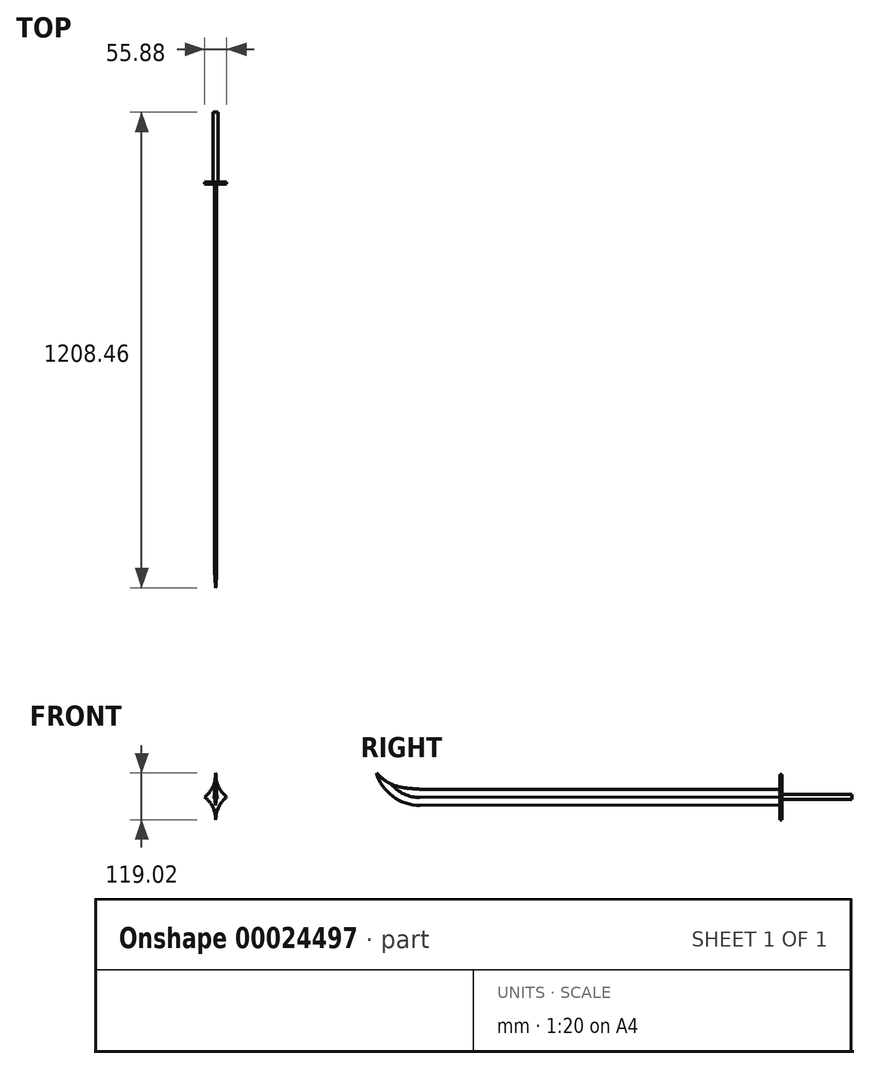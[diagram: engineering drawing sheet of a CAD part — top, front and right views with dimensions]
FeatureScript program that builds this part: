
annotation { "Feature Type Name" : "Feature", "Feature Type Description" : "" }
export const myFeature = defineFeature(function(context is Context, id is Id, definition is map)
    precondition{}
    {
        {
            var Q0;
            Q0=qCreatedBy(makeId("Right.planeOp"),FACE);
            var sketch = newSketch(context, id + "F0", { "sketchPlane" : qUnion([Q0])});
            skArc(sketch, "E0", {"start": v(0, 0) * mm, "mid": v(41.9, -59.69) * mm, "end": v(111.18, -82.52) * mm});
            skLineSegment(sketch, "E1", {"start": v(111.18, -82.52) * mm, "end": v(1025.58, -80.92) * mm});
            skLineSegment(sketch, "E2", {"start": v(111.18, -41.55) * mm, "end": v(1025.58, -41.55) * mm});
            skFitSpline(sketch, "E3", {"points": [v(0, 0) * mm, v(40.72, -30.05) * mm, v(111.18, -41.55) * mm], "startDerivative": vector(79.78, -75.94) * mm, "endDerivative": vector(140.83, -9.08) * mm});
            skLineSegment(sketch, "E4", {"start": v(1025.58, -41.55) * mm, "end": v(1025.58, -80.92) * mm});
            skSolve(sketch);
        }
        {
            var Q0;
            Q0 = qSketchRegion(id + "F0", true);
            extrude(context, id + "F1", {"entities" : qUnion([Q0]), "depth" : 5.08 * mm});
        }
        {
            var Q0;
            Q0=makeQuery(id+"F1.opExtrude","SWEPT_FACE",FACE,{"disambiguationData":[OSD([sQuery(id+"F0.wireOp",EDGE,"E4")])]});
            var sketch = newSketch(context, id + "F2", { "sketchPlane" : qUnion([Q0])});
            skLineSegment(sketch, "E5", {"start": v(-5.08, -61.2) * mm, "end": v(-2.54, -80.88) * mm});
            skLineSegment(sketch, "E6", {"start": v(0, -61.2) * mm, "end": v(-2.54, -80.88) * mm});
            skSolve(sketch);
        }
        {
            var Q0;
            {var subQ0=sQuery(id+"F2.wireOp",EDGE,"E5");Q0=makeQuery(id+"F2.imprint","IMPRINT",FACE,{"disambiguationData":[TD([[makeQuery(id+"F2.imprint","IMPRINT",EDGE,{"derivedFrom":subQ0}),-1.0]])]});}
            var Q1;
            {var subQ0=sQuery(id+"F2.wireOp",EDGE,"E6");Q1=makeQuery(id+"F2.imprint","IMPRINT",FACE,{"disambiguationData":[TD([[makeQuery(id+"F2.imprint","IMPRINT",EDGE,{"derivedFrom":subQ0}),1.0]])]});}
            var Q2;
            Q2=makeQuery(id+"F1.opExtrude","CAP_EDGE",EDGE,{"disambiguationData":[OSD([sQuery(id+"F0.wireOp",EDGE,"E1")])],"isStart":true});
            var Q3;
            Q3=makeQuery(id+"F1.opExtrude","CAP_EDGE",EDGE,{"disambiguationData":[OSD([sQuery(id+"F0.wireOp",EDGE,"E0")])],"isStart":true});
            sweep(context, id + "F3", {"operationType" : NewBodyOperationType.REMOVE, "profiles" : qUnion([Q0, Q1]), "path" : qUnion([Q2, Q3])});
        }
        {
            var Q0;
            Q0=makeQuery(id+"F1.opExtrude","SWEPT_FACE",FACE,{"disambiguationData":[OSD([sQuery(id+"F0.wireOp",EDGE,"E4")])]});
            var sketch = newSketch(context, id + "F4", { "sketchPlane" : qUnion([Q0])});
            skLineSegment(sketch, "E7", {"start": v(-2.54, -41.52) * mm, "end": v(-2.54, -3.42) * mm});
            skLineSegment(sketch, "E8", {"start": v(-2.54, -80.88) * mm, "end": v(-2.54, -118.98) * mm});
            skLineSegment(sketch, "E9", {"start": v(-5.08, -61.2) * mm, "end": v(-30.48, -61.2) * mm});
            skLineSegment(sketch, "E10", {"start": v(0, -61.2) * mm, "end": v(25.4, -61.2) * mm});
            skArc(sketch, "E11", {"start": v(-30.48, -61.2) * mm, "mid": v(-9.9, -35.5) * mm, "end": v(-2.54, -3.42) * mm});
            skArc(sketch, "E12", {"start": v(-2.54, -3.42) * mm, "mid": v(4.81, -35.5) * mm, "end": v(25.4, -61.2) * mm});
            skSolve(sketch);
        }
        {
            var Q0;
            Q0 = qSketchRegion(id + "F4", true);
            var Q1;
            {var subQ2=sQuery(id+"F4.wireOp",EDGE,"E7");Q1=makeQuery(id+"F4.imprint","IMPRINT",FACE,{"disambiguationData":[TD([[makeQuery(id+"F4.imprint","IMPRINT",EDGE,{"derivedFrom":subQ2}),1.0]])]});}
            var Q2;
            {var subQ2=sQuery(id+"F4.wireOp",EDGE,"E7");Q2=makeQuery(id+"F4.imprint","IMPRINT",FACE,{"disambiguationData":[TD([[makeQuery(id+"F4.imprint","IMPRINT",EDGE,{"derivedFrom":subQ2}),-1.0]])]});}
            var Q3;
            {var subQ0=sQuery(id+"F0.wireOp",EDGE,"E4");var subQ3=makeQuery(id+"F1.opExtrude","CAP_EDGE",EDGE,{"disambiguationData":[OSD([subQ0])],"isStart":true});Q3=makeQuery(id+"F4.imprint","IMPRINT",FACE,{"disambiguationData":[TD([[makeQuery(id+"F4.imprint","IMPRINT",EDGE,{"derivedFrom":subQ3}),-1.0]])]});}
            extrude(context, id + "F5", {"entities" : qUnion([Q0, Q1, Q2, Q3]), "depth" : 5.08 * mm});
        }
        {
            var Q0;
            Q0=makeQuery(id+"F5.opExtrude","SWEPT_BODY",BODY,{"disambiguationData":[OSD([sQuery(id+"F0.wireOp",EDGE,"E1"),sQuery(id+"F0.wireOp",EDGE,"E4"),sQuery(id+"F2.wireOp",EDGE,"E5"),sQuery(id+"F2.wireOp",EDGE,"E6"),sQuery(id+"F4.wireOp",EDGE,"E9"),sQuery(id+"F4.wireOp",EDGE,"E10"),sQuery(id+"F4.wireOp",EDGE,"E11"),sQuery(id+"F4.wireOp",EDGE,"E12")])]});
            var Q1;
            Q1=makeQuery(id+"F5.opExtrude","SWEPT_FACE",FACE,{"disambiguationData":[OSD([sQuery(id+"F4.wireOp",EDGE,"E9")])]});
            mirror(context, id + "F6", {"operationType" : NewBodyOperationType.ADD, "entities" : qUnion([Q0]), "mirrorPlane" : qUnion([Q1])});
        }
        {
            var Q0;
            {var subQ0=makeQuery(id+"F5.opExtrude","CAP_FACE",FACE,{"disambiguationData":[OSD([sQuery(id+"F0.wireOp",EDGE,"E1"),sQuery(id+"F0.wireOp",EDGE,"E4"),sQuery(id+"F2.wireOp",EDGE,"E5"),sQuery(id+"F2.wireOp",EDGE,"E6"),sQuery(id+"F4.wireOp",EDGE,"E9"),sQuery(id+"F4.wireOp",EDGE,"E10"),sQuery(id+"F4.wireOp",EDGE,"E11"),sQuery(id+"F4.wireOp",EDGE,"E12")])],"isStart":false});Q0=makeQuery(id+"F6.boolean.opBoolean","MERGE",FACE,{"derivedFrom":[subQ0,makeQuery(id+"F6.opPattern","COPY",FACE,{"derivedFrom":subQ0,"instanceName":"1"})]});}
            var sketch = newSketch(context, id + "F7", { "sketchPlane" : qUnion([Q0])});
            skLineSegment(sketch, "E13", {"start": v(-30.48, -61.2) * mm, "end": v(25.4, -61.2) * mm});
            skCircle(sketch, "E14", {"center": v(-2.54, -61.2) * mm, "radius": 6.35 * mm});
            skSolve(sketch);
        }
        {
            var Q0;
            Q0 = qSketchRegion(id + "F7", true);
            extrude(context, id + "F8", {"entities" : qUnion([Q0]), "operationType" : NewBodyOperationType.ADD, "depth" : 177.8 * mm});
        }
        {
            var Q0;
            Q0=makeQuery(id+"F1.opExtrude","CAP_FACE",FACE,{"disambiguationData":[OSD([sQuery(id+"F0.wireOp",EDGE,"E0"),sQuery(id+"F0.wireOp",EDGE,"E1"),sQuery(id+"F0.wireOp",EDGE,"E2"),sQuery(id+"F0.wireOp",EDGE,"E3"),sQuery(id+"F0.wireOp",EDGE,"E4")])],"isStart":true});
            extrude(context, id + "F9", {"entities" : qUnion([Q0]), "depth" : 0.01 * mm});
        }
        {
            var Q0;
            Q0=makeQuery(id+"F1.opExtrude","CAP_FACE",FACE,{"disambiguationData":[OSD([sQuery(id+"F0.wireOp",EDGE,"E0"),sQuery(id+"F0.wireOp",EDGE,"E1"),sQuery(id+"F0.wireOp",EDGE,"E2"),sQuery(id+"F0.wireOp",EDGE,"E3"),sQuery(id+"F0.wireOp",EDGE,"E4")])],"isStart":false});
            extrude(context, id + "F10", {"entities" : qUnion([Q0]), "depth" : 0.01 * mm});
        }
        {
            var Q0;
            Q0=makeQuery(id+"F1.opExtrude","SWEPT_FACE",FACE,{"disambiguationData":[OSD([sQuery(id+"F0.wireOp",EDGE,"E2")])]});
            extrude(context, id + "F11", {"entities" : qUnion([Q0]), "depth" : 0.01 * mm});
        }
        {
            var Q0;
            Q0=makeQuery(id+"F11.opExtrude","SWEPT_FACE",FACE,{"disambiguationData":[OSD([sQuery(id+"F0.wireOp",EDGE,"E2"),sQuery(id+"F0.wireOp",EDGE,"E3")])]});
            var Q1;
            Q1=makeQuery(id+"F1.opExtrude","CAP_EDGE",EDGE,{"disambiguationData":[OSD([sQuery(id+"F0.wireOp",EDGE,"E3")])],"isStart":false});
            sweep(context, id + "F12", {"operationType" : NewBodyOperationType.ADD, "profiles" : qUnion([Q0]), "path" : qUnion([Q1])});
        }
    });
